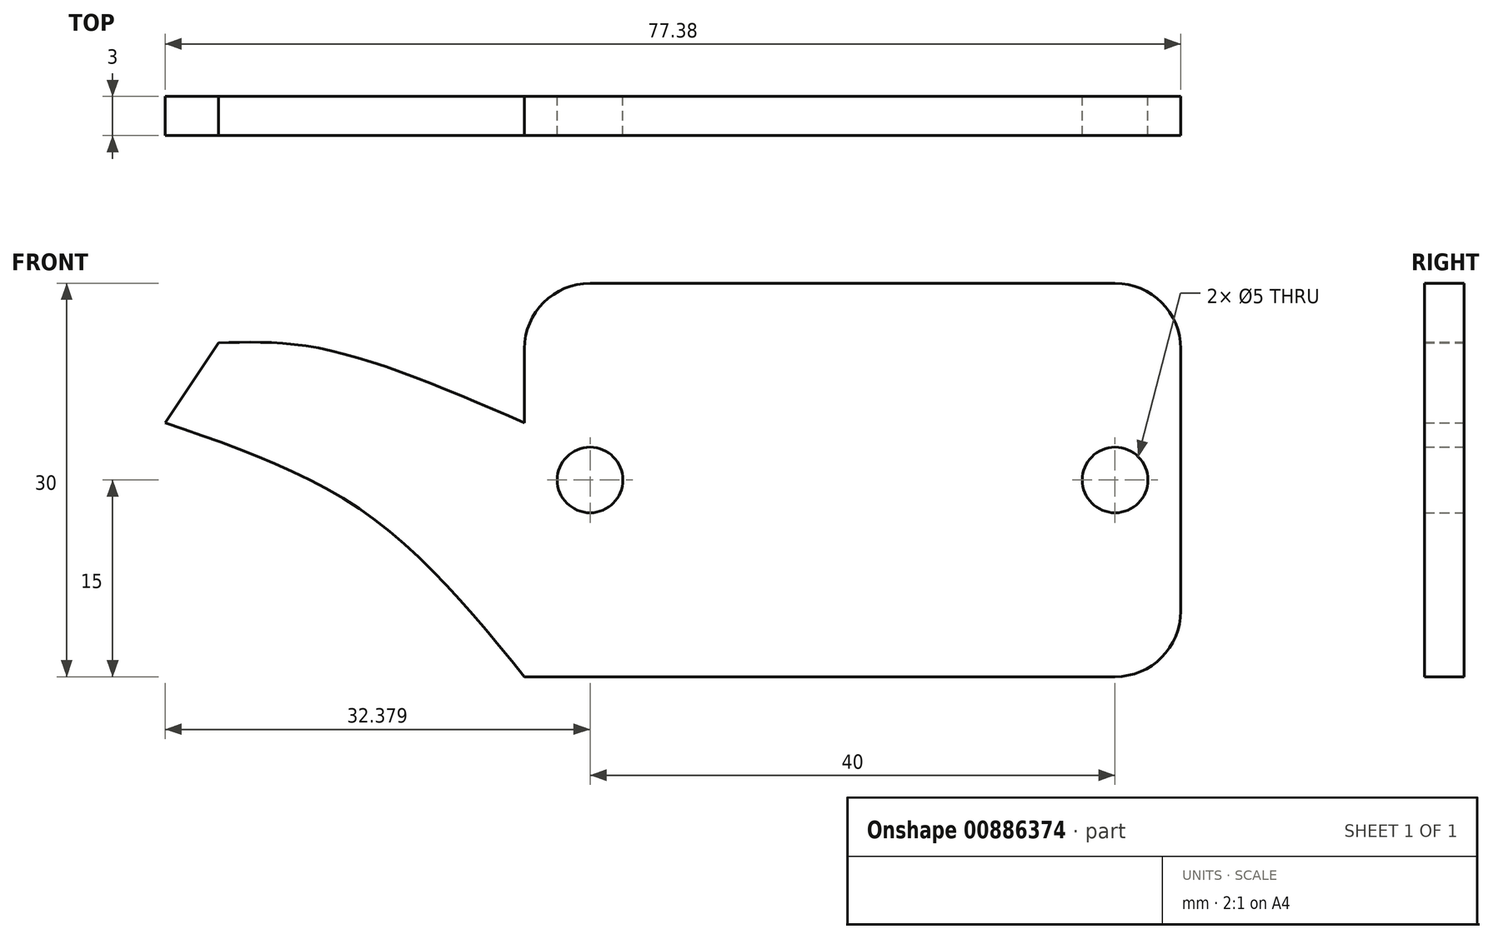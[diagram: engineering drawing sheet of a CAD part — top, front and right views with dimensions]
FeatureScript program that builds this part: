
annotation { "Feature Type Name" : "Feature", "Feature Type Description" : "" }
export const myFeature = defineFeature(function(context is Context, id is Id, definition is map)
    precondition{}
    {
        {
            var Q0;
            Q0=qCreatedBy(makeId("Front.planeOp"),FACE);
            var sketch = newSketch(context, id + "F0", { "sketchPlane" : qUnion([Q0])});
            skLineSegment(sketch, "E0.bottom", {"start": v(-10.9, 15) * mm, "end": v(29.1, 15) * mm});
            skLineSegment(sketch, "E0.top", {"start": v(-15.9, -15) * mm, "end": v(29.1, -15) * mm});
            skLineSegment(sketch, "E0.left", {"start": v(-15.9, 10) * mm, "end": v(-15.9, 4.37) * mm});
            skLineSegment(sketch, "E0.right", {"start": v(34.1, 10) * mm, "end": v(34.1, -10) * mm});
            skCircle(sketch, "E1", {"center": v(-10.9, 0) * mm, "radius": 2.5 * mm});
            skCircle(sketch, "E2", {"center": v(29.1, 0) * mm, "radius": 2.5 * mm});
            skPoint(sketch, "E3.visualSharp", {"position": v(-15.9, 15) * mm});
            skArc(sketch, "E3.filletArc", {"start": v(-10.9, 15) * mm, "mid": v(-14.44, 13.54) * mm, "end": v(-15.9, 10) * mm});
            skPoint(sketch, "E4.visualSharp", {"position": v(34.1, 15) * mm});
            skArc(sketch, "E4.filletArc", {"start": v(34.1, 10) * mm, "mid": v(32.63, 13.54) * mm, "end": v(29.1, 15) * mm});
            skPoint(sketch, "E5.visualSharp", {"position": v(34.1, -15) * mm});
            skArc(sketch, "E5.filletArc", {"start": v(29.1, -15) * mm, "mid": v(32.63, -13.54) * mm, "end": v(34.1, -10) * mm});
            skPoint(sketch, "E6.1.internal.snap0", {"position": v(-15.9, -2.5) * mm});
            skFitSpline(sketch, "E6", {"points": [v(-15.9, -15) * mm, v(-28.04, -2.5) * mm, v(-43.28, 4.37) * mm], "startDerivative": vector(-22.31, 27.49) * mm, "endDerivative": vector(-32.48, 11.19) * mm});
            skFitSpline(sketch, "E7", {"points": [v(-15.9, 4.37) * mm, v(-31.09, 9.95) * mm, v(-39.21, 10.46) * mm], "startDerivative": vector(-27.82, 11.99) * mm, "endDerivative": vector(-18.26, -0.5) * mm});
            skLineSegment(sketch, "E8", {"start": v(-39.21, 10.46) * mm, "end": v(-43.28, 4.37) * mm});
            skSolve(sketch);
        }
        {
            var Q0;
            Q0 = qSketchRegion(id + "F0", true);
            extrude(context, id + "F1", {"entities" : qUnion([Q0]), "depth" : 3 * mm, "offsetDistance" : 25 * mm});
        }
    });
